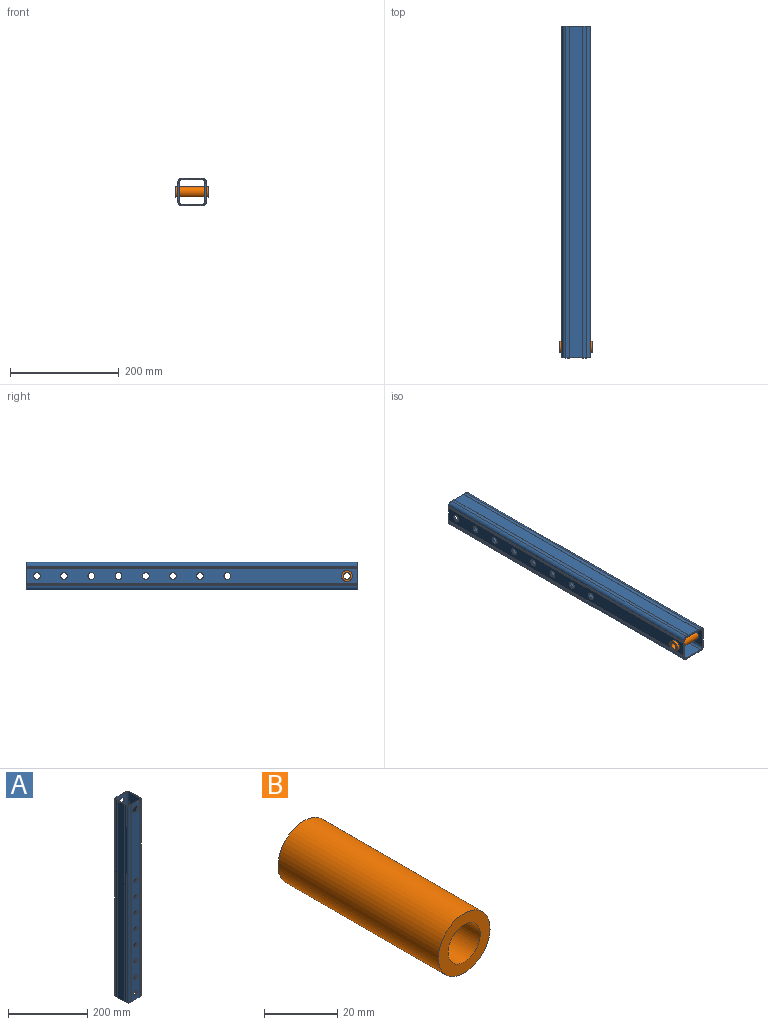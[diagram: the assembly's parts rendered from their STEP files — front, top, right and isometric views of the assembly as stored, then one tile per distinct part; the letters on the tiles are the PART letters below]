
ASSEMBLY  parts=2 mates=1
PART A: 60 faces, bbox 51x52.3x610 mm
  f0: plane 52.3x51mm, normal (0,0,1), area 515.2mm2, adj f2,f3,f4,f5,f15,f25,f26,f27
  f1: plane 52.3x51mm, normal (0,0,-1), area 515.2mm2, adj f2,f3,f4,f5,f15,f25,f26,f27
  f2: plane 610x28mm, normal (0,-1,0), area 15784.1mm2, adj f0,f1,f16,f17,f18,f19,f20,f21
  f3: plane 610x6.5mm, normal (1,0,0), area 3965mm2, adj f0,f1,f28,f42
  f4: plane 610x6.5mm, normal (-1,0,0), area 3965mm2, adj f0,f1,f27,f40
  f5: plane 610x28mm, normal (0,1,0), area 15784.1mm2, adj f0,f1,f6,f7,f8,f9,f10,f11
  f6: cylinder r=6.25mm len=12.5mm, axis (0,-1,0), area 113.9mm2, adj f5,f31
  f7: cylinder r=6.25mm len=12.5mm, axis (0,-1,0), area 113.9mm2, adj f5,f31
  f8: cylinder r=6.25mm len=12.5mm, axis (0,-1,0), area 113.9mm2, adj f5,f31
  f9: cylinder r=6.25mm len=12.5mm, axis (0,-1,0), area 113.9mm2, adj f5,f31
  f10: cylinder r=6.25mm len=12.5mm, axis (0,-1,0), area 113.9mm2, adj f5,f31
  f11: cylinder r=6.25mm len=12.5mm, axis (0,-1,0), area 113.9mm2, adj f5,f31
  f12: cylinder r=6.25mm len=12.5mm, axis (0,-1,0), area 113.9mm2, adj f5,f31
  f13: cylinder r=6.25mm len=12.5mm, axis (0,-1,0), area 113.9mm2, adj f5,f31
  f14: cylinder r=10mm len=20mm, axis (0,-1,0), area 182.2mm2, adj f5,f31
  f15: plane 610x6.5mm, normal (1,0,0), area 3965mm2, adj f0,f1,f26,f43
  f16: cylinder r=6.25mm len=12.5mm, axis (0,-1,0), area 113.9mm2, adj f2,f36
  f17: cylinder r=6.25mm len=12.5mm, axis (0,-1,0), area 113.9mm2, adj f2,f36
  f18: cylinder r=6.25mm len=12.5mm, axis (0,-1,0), area 113.9mm2, adj f2,f36
  f19: cylinder r=6.25mm len=12.5mm, axis (0,-1,0), area 113.9mm2, adj f2,f36
  f20: cylinder r=6.25mm len=12.5mm, axis (0,-1,0), area 113.9mm2, adj f2,f36
  f21: cylinder r=6.25mm len=12.5mm, axis (0,-1,0), area 113.9mm2, adj f2,f36
  f22: cylinder r=6.25mm len=12.5mm, axis (0,-1,0), area 113.9mm2, adj f2,f36
  f23: cylinder r=6.25mm len=12.5mm, axis (0,-1,0), area 113.9mm2, adj f2,f36
  f24: cylinder r=10mm len=20mm, axis (0,-1,0), area 182.2mm2, adj f2,f36
  f25: plane 610x6.5mm, normal (-1,0,0), area 3965mm2, adj f0,f1,f29,f38
  f26: cylinder r=7.5mm len=610mm, axis (0,0,-1), area 7186.4mm2, adj f0,f1,f15,f52
  f27: cylinder r=7.5mm len=610mm, axis (0,0,1), area 7186.4mm2, adj f0,f1,f4,f46
  f28: cylinder r=7.5mm len=610mm, axis (0,0,1), area 7186.4mm2, adj f0,f1,f3,f48
  f29: cylinder r=7.5mm len=610mm, axis (0,0,-1), area 7186.4mm2, adj f0,f1,f25,f58
  f30: cylinder r=4.6mm len=610mm, axis (0,0,1), area 4407.7mm2, adj f0,f1,f31,f35
  f31: plane 610x36mm, normal (0,-1,0), area 20664.1mm2, adj f0,f1,f6,f7,f8,f9,f10,f11
  f32: cylinder r=4.6mm len=610mm, axis (0,0,1), area 4407.7mm2, adj f0,f1,f31,f33
  f33: plane 610x37.3mm, normal (1,0,0), area 22753mm2, adj f0,f1,f32,f34
  f34: cylinder r=4.6mm len=610mm, axis (0,0,1), area 4407.7mm2, adj f0,f1,f33,f36
  f35: plane 610x37.3mm, normal (-1,0,0), area 22753mm2, adj f0,f1,f30,f37
  f36: plane 610x36mm, normal (0,1,0), area 20664.1mm2, adj f0,f1,f16,f17,f18,f19,f20,f21
  f37: cylinder r=4.6mm len=610mm, axis (0,0,1), area 4407.7mm2, adj f0,f1,f35,f36
  f38: plane 610x0.25mm, normal (0,-1,0), area 152.5mm2, adj f0,f1,f25,f39
  f39: plane 610x24.3mm, normal (-1,0,0), area 14823mm2, adj f0,f1,f38,f40
  f40: plane 610x0.25mm, normal (0,1,0), area 152.5mm2, adj f0,f1,f4,f39
  f41: plane 610x24.3mm, normal (1,0,0), area 14823mm2, adj f0,f1,f42,f43
  f42: plane 610x0.25mm, normal (0,-1,0), area 152.5mm2, adj f0,f1,f3,f41
  f43: plane 610x0.25mm, normal (0,1,0), area 152.5mm2, adj f0,f1,f15,f41
  f44: plane 610x1mm, normal (-0.71,-0.71,0), area 862.7mm2, adj f0,f1,f45,f53
  f45: plane 610x1mm, normal (0.71,-0.71,0), area 862.7mm2, adj f0,f1,f2,f44
  f46: plane 610x1mm, normal (0.71,-0.71,0), area 862.7mm2, adj f0,f1,f27,f47
  f47: plane 610x1mm, normal (-0.71,-0.71,0), area 862.7mm2, adj f0,f1,f46,f54
  f48: plane 610x1mm, normal (-0.71,0.71,0), area 862.7mm2, adj f0,f1,f28,f49
  f49: plane 610x1mm, normal (0.71,0.71,0), area 862.7mm2, adj f0,f1,f48,f56
  f50: plane 610x1mm, normal (0.71,0.71,0), area 862.7mm2, adj f0,f1,f51,f59
  f51: plane 610x1mm, normal (-0.71,0.71,0), area 862.7mm2, adj f0,f1,f5,f50
  f52: plane 610x1mm, normal (-0.71,-0.71,0), area 862.7mm2, adj f0,f1,f26,f53
  f53: plane 610x1mm, normal (0.71,-0.71,0), area 862.7mm2, adj f0,f1,f44,f52
  f54: plane 610x1mm, normal (0.71,-0.71,0), area 862.7mm2, adj f0,f1,f47,f55
  f55: plane 610x1mm, normal (-0.71,-0.71,0), area 862.7mm2, adj f0,f1,f2,f54
  f56: plane 610x1mm, normal (-0.71,0.71,0), area 862.7mm2, adj f0,f1,f49,f57
  f57: plane 610x1mm, normal (0.71,0.71,0), area 862.7mm2, adj f0,f1,f5,f56
  f58: plane 610x1mm, normal (0.71,0.71,0), area 862.7mm2, adj f0,f1,f29,f59
  f59: plane 610x1mm, normal (-0.71,0.71,0), area 862.7mm2, adj f0,f1,f50,f58
PART B: 4 faces, bbox 20x62x20 mm
  f0: cylinder r=6.25mm len=62mm, axis (0,1,0), area 2434.7mm2, adj f2,f3
  f1: cylinder r=10mm len=62mm, axis (0,1,0), area 3895.6mm2, adj f2,f3
  f2: plane 20x20mm, normal (0,-1,0), area 191.4mm2, adj f0,f1
  f3: plane 20x20mm, normal (0,1,0), area 191.4mm2, adj f0,f1
PLACE A rot(axis=(0.58,0.58,-0.58),120deg) t=(30,330.32,-274.5)mm
PLACE B rot(axis=(0,0,-1),90deg) t=(689.85,-864.18,-920)mm
MATE fastened B.f0 <-> A.f14  axis (-1,0,0) through (-31.15,-589.68,0)mm
